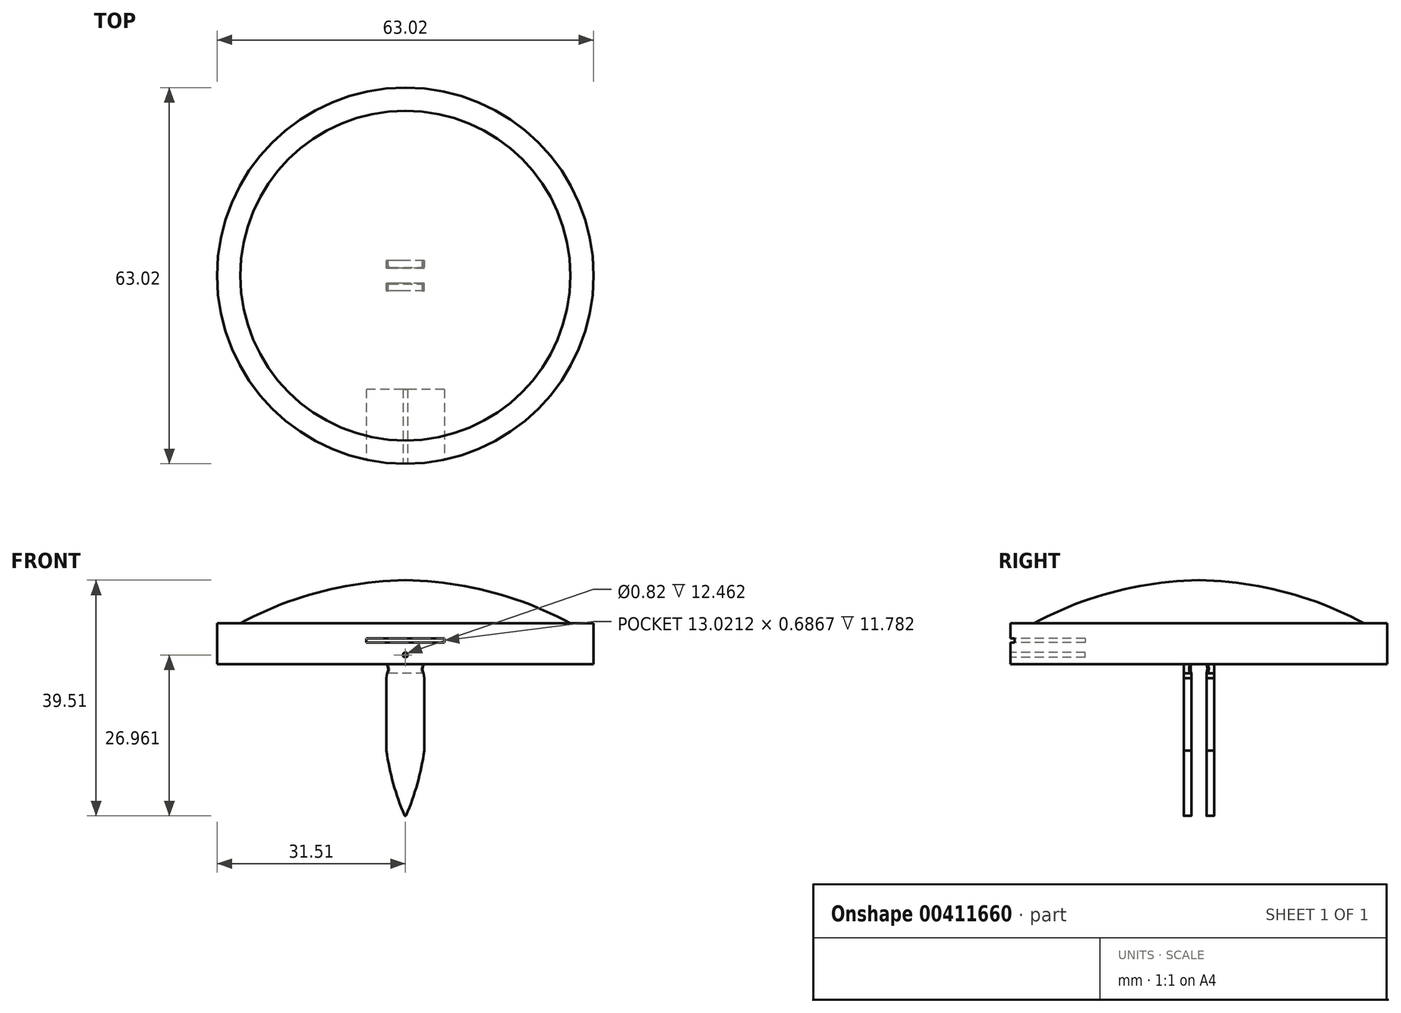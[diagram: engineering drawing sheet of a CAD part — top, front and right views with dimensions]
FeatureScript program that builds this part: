
annotation { "Feature Type Name" : "Feature", "Feature Type Description" : "" }
export const myFeature = defineFeature(function(context is Context, id is Id, definition is map)
    precondition{}
    {
        {
            var Q0;
            Q0=qCreatedBy(makeId("Top.planeOp"),FACE);
            var sketch = newSketch(context, id + "F0", { "sketchPlane" : qUnion([Q0])});
            skCircle(sketch, "E0", {"center": v(0, 0) * mm, "radius": 31.51 * mm});
            skSolve(sketch);
        }
        {
            var Q0;
            Q0=makeQuery(id+"F0.imprint","IMPRINT",FACE,{"disambiguationData":[TD([[makeQuery(id+"F0.imprint","IMPRINT",EDGE,{"derivedFrom":sQuery(id+"F0.wireOp",EDGE,"E0")}),1.0]])]});
            var Q1;
            Q1=sQuery(id+"F0.wireOp",EDGE,"E0");
            extrude(context, id + "F1", {"entities" : qUnion([Q0]), "surfaceEntities" : qUnion([Q1]), "depth" : 25.4 * mm});
        }
        {
            var Q0;
            Q0=qCreatedBy(makeId("Front.planeOp"),FACE);
            var sketch = newSketch(context, id + "F2", { "sketchPlane" : qUnion([Q0])});
            skLineSegment(sketch, "E1", {"start": v(0, 14.1) * mm, "end": v(0, 28.1) * mm});
            skLineSegment(sketch, "E2", {"start": v(0, 28.1) * mm, "end": v(33.46, 28.1) * mm});
            skLineSegment(sketch, "E3", {"start": v(33.46, 28.1) * mm, "end": v(33.46, 6.87) * mm});
            skLineSegment(sketch, "E4", {"start": v(33.46, 6.87) * mm, "end": v(27.62, 6.87) * mm});
            skArc(sketch, "E5", {"start": v(27.62, 6.87) * mm, "mid": v(14.25, 12.15) * mm, "end": v(0, 14.1) * mm});
            skSolve(sketch);
        }
        {
            var Q0;
            Q0=makeQuery(id+"F2.imprint","IMPRINT",FACE,{"disambiguationData":[TD([[makeQuery(id+"F2.imprint","IMPRINT",EDGE,{"derivedFrom":sQuery(id+"F2.wireOp",EDGE,"E1")}),-1.0]])]});
            var Q1;
            Q1=sQuery(id+"F2.wireOp",EDGE,"E1");
            revolve(context, id + "F3", {"operationType" : NewBodyOperationType.REMOVE, "entities" : qUnion([Q0]), "axis" : qUnion([Q1]), "revolveType" : RevolveType.FULL, "oppositeDirection" : true});
        }
        {
            var Q0;
            Q0=qCreatedBy(makeId("Top.planeOp"),FACE);
            var sketch = newSketch(context, id + "F4", { "sketchPlane" : qUnion([Q0])});
            skLineSegment(sketch, "E6.bottom", {"start": v(3.18, -2.54) * mm, "end": v(-3.18, -2.54) * mm});
            skLineSegment(sketch, "E6.top", {"start": v(3.17, -1.27) * mm, "end": v(-3.17, -1.27) * mm});
            skLineSegment(sketch, "E6.left", {"start": v(3.18, -2.54) * mm, "end": v(3.18, -1.27) * mm});
            skLineSegment(sketch, "E6.right", {"start": v(-3.18, -2.54) * mm, "end": v(-3.18, -1.27) * mm});
            skPoint(sketch, "E6.middle", {"position": v(0, -1.9) * mm});
            skLineSegment(sketch, "E7.MirrorCS", {"start": v(3.17, 1.27) * mm, "end": v(-3.17, 1.27) * mm});
            skLineSegment(sketch, "E8.MirrorCS", {"start": v(-3.18, 2.54) * mm, "end": v(-3.18, 1.27) * mm});
            skLineSegment(sketch, "E9.MirrorCS", {"start": v(3.18, 2.54) * mm, "end": v(-3.18, 2.54) * mm});
            skLineSegment(sketch, "E10.MirrorCS", {"start": v(3.18, 2.54) * mm, "end": v(3.18, 1.27) * mm});
            skSolve(sketch);
        }
        {
            var Q0;
            Q0 = qSketchRegion(id + "F4", true);
            extrude(context, id + "F5", {"entities" : qUnion([Q0]), "operationType" : NewBodyOperationType.ADD, "oppositeDirection" : true, "depth" : 25.4 * mm});
        }
        {
            var Q0;
            Q0=qCreatedBy(makeId("Front.planeOp"),FACE);
            var sketch = newSketch(context, id + "F6", { "sketchPlane" : qUnion([Q0])});
            skArc(sketch, "E11", {"start": v(3.17, 0) * mm, "mid": v(2.88, -0.72) * mm, "end": v(3.05, -1.49) * mm});
            skArc(sketch, "E12", {"start": v(0, -25.64) * mm, "mid": v(3.26, -13.79) * mm, "end": v(3.05, -1.49) * mm});
            skArc(sketch, "E13.MirrorCS", {"start": v(0, -25.64) * mm, "mid": v(-3.26, -13.79) * mm, "end": v(-3.05, -1.49) * mm});
            skArc(sketch, "E14.MirrorCS", {"start": v(-3.17, 0) * mm, "mid": v(-2.88, -0.72) * mm, "end": v(-3.05, -1.49) * mm});
            skLineSegment(sketch, "E15", {"start": v(3.17, 0) * mm, "end": v(7.5, 0) * mm});
            skLineSegment(sketch, "E16", {"start": v(7.5, 0) * mm, "end": v(7.5, -28.21) * mm});
            skLineSegment(sketch, "E17", {"start": v(7.5, -28.21) * mm, "end": v(-8.46, -28.21) * mm});
            skLineSegment(sketch, "E18", {"start": v(-8.46, -28.21) * mm, "end": v(-8.46, 0) * mm});
            skLineSegment(sketch, "E19", {"start": v(-8.46, 0) * mm, "end": v(-3.17, 0) * mm});
            skSolve(sketch);
        }
        {
            var Q0;
            Q0=makeQuery(id+"F6.imprint","IMPRINT",FACE,{"disambiguationData":[TD([[makeQuery(id+"F6.imprint","IMPRINT",EDGE,{"derivedFrom":sQuery(id+"F6.wireOp",EDGE,"E11")}),1.0]])]});
            extrude(context, id + "F7", {"entities" : qUnion([Q0]), "operationType" : NewBodyOperationType.REMOVE, "depth" : 25.4 * mm, "hasSecondDirection" : true, "secondDirectionOppositeDirection" : true, "secondDirectionDepth" : 25.4 * mm});
        }
        {
            var Q0;
            Q0=qCreatedBy(makeId("Right.planeOp"),FACE);
            var sketch = newSketch(context, id + "F8", { "sketchPlane" : qUnion([Q0])});
            skArc(sketch, "E20", {"start": v(1.27, -1.46) * mm, "mid": v(1.4, -0.73) * mm, "end": v(1.27, 0) * mm});
            skArc(sketch, "E21.MirrorCS", {"start": v(-1.27, -1.46) * mm, "mid": v(-1.4, -0.73) * mm, "end": v(-1.27, 0) * mm});
            skLineSegment(sketch, "E22", {"start": v(1.27, 0) * mm, "end": v(-1.27, 0) * mm});
            skLineSegment(sketch, "E23", {"start": v(-1.27, -1.46) * mm, "end": v(1.27, -1.46) * mm});
            skSolve(sketch);
        }
        {
            var Q0;
            Q0 = qSketchRegion(id + "F8", true);
            extrude(context, id + "F9", {"entities" : qUnion([Q0]), "operationType" : NewBodyOperationType.REMOVE, "oppositeDirection" : true, "depth" : 25.4 * mm, "hasSecondDirection" : true, "secondDirectionOppositeDirection" : false, "secondDirectionDepth" : 25.4 * mm});
        }
        {
            var Q0;
            Q0=makeQuery(id+"F7.boolean.opBoolean","INTERSECT",EDGE,{"derivedFrom":[makeQuery(id+"F5.opExtrude","CAP_FACE",FACE,{"disambiguationData":[OSD([sQuery(id+"F4.wireOp",EDGE,"E6.bottom"),sQuery(id+"F4.wireOp",EDGE,"E6.top"),sQuery(id+"F4.wireOp",EDGE,"E6.left"),sQuery(id+"F4.wireOp",EDGE,"E6.right")])],"isStart":false}),makeQuery(id+"F7.opExtrude","SWEPT_FACE",FACE,{"disambiguationData":[OSD([sQuery(id+"F6.wireOp",EDGE,"E13.MirrorCS")])]})]});
            var Q1;
            Q1=makeQuery(id+"F7.boolean.opBoolean","INTERSECT",EDGE,{"derivedFrom":[makeQuery(id+"F5.opExtrude","CAP_FACE",FACE,{"disambiguationData":[OSD([sQuery(id+"F4.wireOp",EDGE,"E6.bottom"),sQuery(id+"F4.wireOp",EDGE,"E6.top"),sQuery(id+"F4.wireOp",EDGE,"E6.left"),sQuery(id+"F4.wireOp",EDGE,"E6.right")])],"isStart":false}),makeQuery(id+"F7.opExtrude","SWEPT_FACE",FACE,{"disambiguationData":[OSD([sQuery(id+"F6.wireOp",EDGE,"E12")])]})]});
            var Q2;
            Q2=makeQuery(id+"F7.boolean.opBoolean","INTERSECT",EDGE,{"derivedFrom":[makeQuery(id+"F5.opExtrude","CAP_FACE",FACE,{"disambiguationData":[OSD([sQuery(id+"F4.wireOp",EDGE,"E7.MirrorCS"),sQuery(id+"F4.wireOp",EDGE,"E8.MirrorCS"),sQuery(id+"F4.wireOp",EDGE,"E9.MirrorCS"),sQuery(id+"F4.wireOp",EDGE,"E10.MirrorCS")])],"isStart":false}),makeQuery(id+"F7.opExtrude","SWEPT_FACE",FACE,{"disambiguationData":[OSD([sQuery(id+"F6.wireOp",EDGE,"E13.MirrorCS")])]})]});
            var Q3;
            Q3=makeQuery(id+"F7.boolean.opBoolean","INTERSECT",EDGE,{"derivedFrom":[makeQuery(id+"F5.opExtrude","CAP_FACE",FACE,{"disambiguationData":[OSD([sQuery(id+"F4.wireOp",EDGE,"E7.MirrorCS"),sQuery(id+"F4.wireOp",EDGE,"E8.MirrorCS"),sQuery(id+"F4.wireOp",EDGE,"E9.MirrorCS"),sQuery(id+"F4.wireOp",EDGE,"E10.MirrorCS")])],"isStart":false}),makeQuery(id+"F7.opExtrude","SWEPT_FACE",FACE,{"disambiguationData":[OSD([sQuery(id+"F6.wireOp",EDGE,"E12")])]})]});
            fillet(context, id + "F10", {"entities" : qUnion([Q0, Q1, Q2, Q3]), "radius" : 0.13 * mm, "tangentPropagation" : true, "allowEdgeOverflow" : false});
        }
        {
            var Q0;
            Q0=makeQuery(id+"F9.boolean.opBoolean","INTERSECT",EDGE,{"derivedFrom":[makeQuery(id+"F7.boolean.opBoolean","COPY",FACE,{"disambiguationData":[TD([makeQuery(id+"F5.opExtrude","SWEPT_FACE",FACE,{"disambiguationData":[OSD([sQuery(id+"F4.wireOp",EDGE,"E6.bottom")])]})])],"derivedFrom":makeQuery(id+"F7.opExtrude","SWEPT_FACE",FACE,{"disambiguationData":[OSD([sQuery(id+"F6.wireOp",EDGE,"E14.MirrorCS")])]})}),makeQuery(id+"F9.opExtrude","SWEPT_FACE",FACE,{"disambiguationData":[OSD([sQuery(id+"F8.wireOp",EDGE,"E21.MirrorCS")])]})]});
            var Q1;
            Q1=makeQuery(id+"F9.boolean.opBoolean","INTERSECT",EDGE,{"derivedFrom":[makeQuery(id+"F7.boolean.opBoolean","COPY",FACE,{"disambiguationData":[TD([makeQuery(id+"F5.opExtrude","SWEPT_FACE",FACE,{"disambiguationData":[OSD([sQuery(id+"F4.wireOp",EDGE,"E7.MirrorCS")])]})])],"derivedFrom":makeQuery(id+"F7.opExtrude","SWEPT_FACE",FACE,{"disambiguationData":[OSD([sQuery(id+"F6.wireOp",EDGE,"E11")])]})}),makeQuery(id+"F9.opExtrude","SWEPT_FACE",FACE,{"disambiguationData":[OSD([sQuery(id+"F8.wireOp",EDGE,"E20")])]})]});
            var Q2;
            Q2=makeQuery(id+"F9.boolean.opBoolean","INTERSECT",EDGE,{"derivedFrom":[makeQuery(id+"F7.boolean.opBoolean","COPY",FACE,{"disambiguationData":[TD([makeQuery(id+"F5.opExtrude","SWEPT_FACE",FACE,{"disambiguationData":[OSD([sQuery(id+"F4.wireOp",EDGE,"E6.bottom")])]})])],"derivedFrom":makeQuery(id+"F7.opExtrude","SWEPT_FACE",FACE,{"disambiguationData":[OSD([sQuery(id+"F6.wireOp",EDGE,"E11")])]})}),makeQuery(id+"F9.opExtrude","SWEPT_FACE",FACE,{"disambiguationData":[OSD([sQuery(id+"F8.wireOp",EDGE,"E21.MirrorCS")])]})]});
            var Q3;
            Q3=makeQuery(id+"F9.boolean.opBoolean","INTERSECT",EDGE,{"derivedFrom":[makeQuery(id+"F7.boolean.opBoolean","COPY",FACE,{"disambiguationData":[TD([makeQuery(id+"F5.opExtrude","SWEPT_FACE",FACE,{"disambiguationData":[OSD([sQuery(id+"F4.wireOp",EDGE,"E7.MirrorCS")])]})])],"derivedFrom":makeQuery(id+"F7.opExtrude","SWEPT_FACE",FACE,{"disambiguationData":[OSD([sQuery(id+"F6.wireOp",EDGE,"E14.MirrorCS")])]})}),makeQuery(id+"F9.opExtrude","SWEPT_FACE",FACE,{"disambiguationData":[OSD([sQuery(id+"F8.wireOp",EDGE,"E20")])]})]});
            fillet(context, id + "F11", {"entities" : qUnion([Q0, Q1, Q2, Q3]), "radius" : 0.25 * mm, "tangentPropagation" : true, "allowEdgeOverflow" : false});
        }
        {
            var Q0;
            Q0=qCreatedBy(makeId("Front.planeOp"),FACE);
            cPlane(context, id + "F12", {"entities" : qUnion([Q0]), "cplaneType" : CPlaneType.OFFSET, "offset" : 31.75 * mm, "width" : 152.4 * mm, "height" : 152.4 * mm});
        }
        {
            var Q0;
            Q0=qCreatedBy(id+"F12.planeOp",FACE);
            var sketch = newSketch(context, id + "F13", { "sketchPlane" : qUnion([Q0])});
            skLineSegment(sketch, "E24.bottom", {"start": v(6.51, 4.36) * mm, "end": v(-6.51, 4.36) * mm});
            skLineSegment(sketch, "E24.top", {"start": v(6.51, 3.67) * mm, "end": v(-6.51, 3.67) * mm});
            skLineSegment(sketch, "E24.left", {"start": v(6.51, 4.36) * mm, "end": v(6.51, 3.67) * mm});
            skLineSegment(sketch, "E24.right", {"start": v(-6.51, 4.36) * mm, "end": v(-6.51, 3.67) * mm});
            skPoint(sketch, "E24.middle", {"position": v(0, 4.01) * mm});
            skCircle(sketch, "E25", {"center": v(0, 1.56) * mm, "radius": 0.41 * mm});
            skSolve(sketch);
        }
        {
            var Q0;
            Q0=makeQuery(id+"F13.imprint","IMPRINT",FACE,{"disambiguationData":[TD([[makeQuery(id+"F13.imprint","IMPRINT",EDGE,{"derivedFrom":sQuery(id+"F13.wireOp",EDGE,"E24.bottom")}),1.0]])]});
            var Q1;
            Q1=makeQuery(id+"F13.imprint","IMPRINT",FACE,{"disambiguationData":[TD([[makeQuery(id+"F13.imprint","IMPRINT",EDGE,{"derivedFrom":sQuery(id+"F13.wireOp",EDGE,"E25")}),1.0]])]});
            extrude(context, id + "F14", {"entities" : qUnion([Q0, Q1]), "operationType" : NewBodyOperationType.REMOVE, "oppositeDirection" : true, "depth" : 12.7 * mm});
        }
    });
